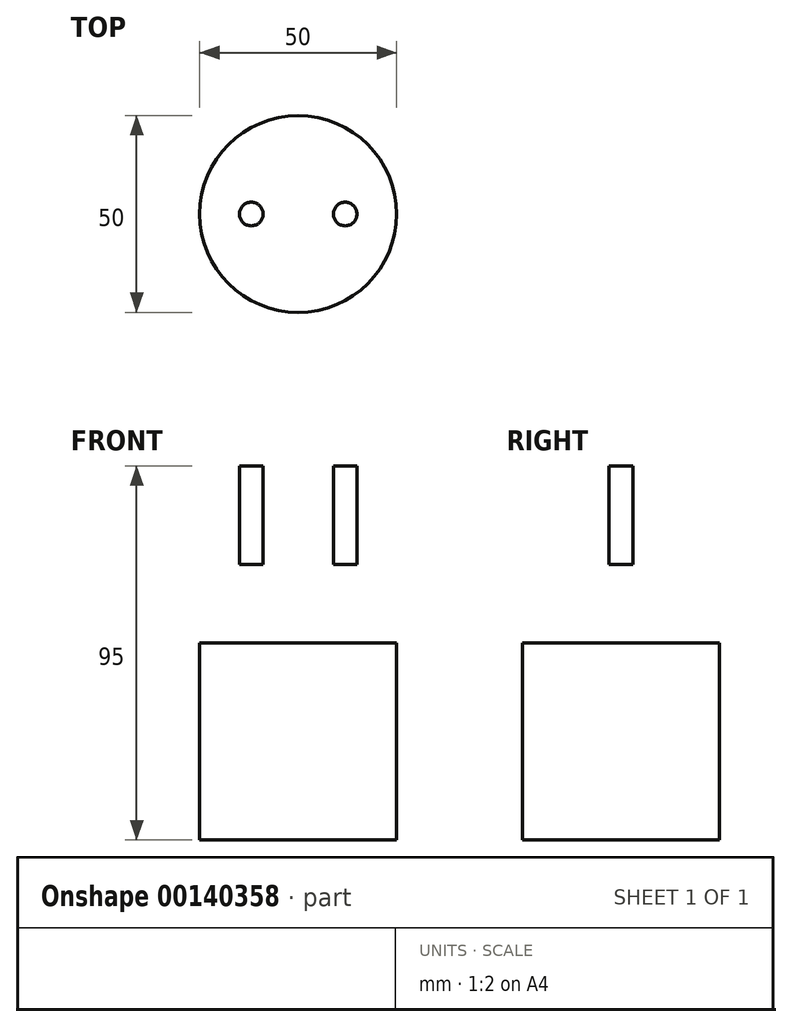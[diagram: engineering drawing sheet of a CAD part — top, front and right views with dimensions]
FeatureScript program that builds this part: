
annotation { "Feature Type Name" : "Feature", "Feature Type Description" : "" }
export const myFeature = defineFeature(function(context is Context, id is Id, definition is map)
    precondition{}
    {
        {
            var Q0;
            Q0=qCreatedBy(makeId("Top.planeOp"),FACE);
            cPlane(context, id + "F0", {"entities" : qUnion([Q0]), "cplaneType" : CPlaneType.OFFSET, "offset" : 25 * mm, "width" : 150 * mm, "height" : 150 * mm});
        }
        {
            var Q0;
            Q0=qCreatedBy(id+"F0.planeOp",FACE);
            var sketch = newSketch(context, id + "F1", { "sketchPlane" : qUnion([Q0])});
            skCircle(sketch, "E0", {"center": v(0, 0) * mm, "radius": 25 * mm});
            skSolve(sketch);
        }
        {
            var Q0;
            Q0 = qSketchRegion(id + "F1", true);
            extrude(context, id + "F2", {"entities" : qUnion([Q0]), "oppositeDirection" : true, "depth" : 50 * mm});
        }
        {
            var Q0;
            Q0=makeQuery(id+"F2.opExtrude","CAP_FACE",FACE,{"disambiguationData":[OSD([sQuery(id+"F1.wireOp",EDGE,"E0")])],"isStart":true});
            cPlane(context, id + "F3", {"entities" : qUnion([Q0]), "cplaneType" : CPlaneType.OFFSET, "offset" : 20 * mm, "width" : 150 * mm, "height" : 150 * mm});
        }
        {
            var Q0;
            Q0=qCreatedBy(id+"F3.planeOp",FACE);
            var sketch = newSketch(context, id + "F4", { "sketchPlane" : qUnion([Q0])});
            skCircle(sketch, "E1", {"center": v(-11.93, 0) * mm, "radius": 3 * mm});
            skCircle(sketch, "E2.MirrorC", {"center": v(11.93, 0) * mm, "radius": 3 * mm});
            skSolve(sketch);
        }
        {
            var Q0;
            Q0 = qSketchRegion(id + "F4", true);
            extrude(context, id + "F5", {"entities" : qUnion([Q0]), "operationType" : NewBodyOperationType.ADD, "depth" : 25 * mm});
        }
    });
